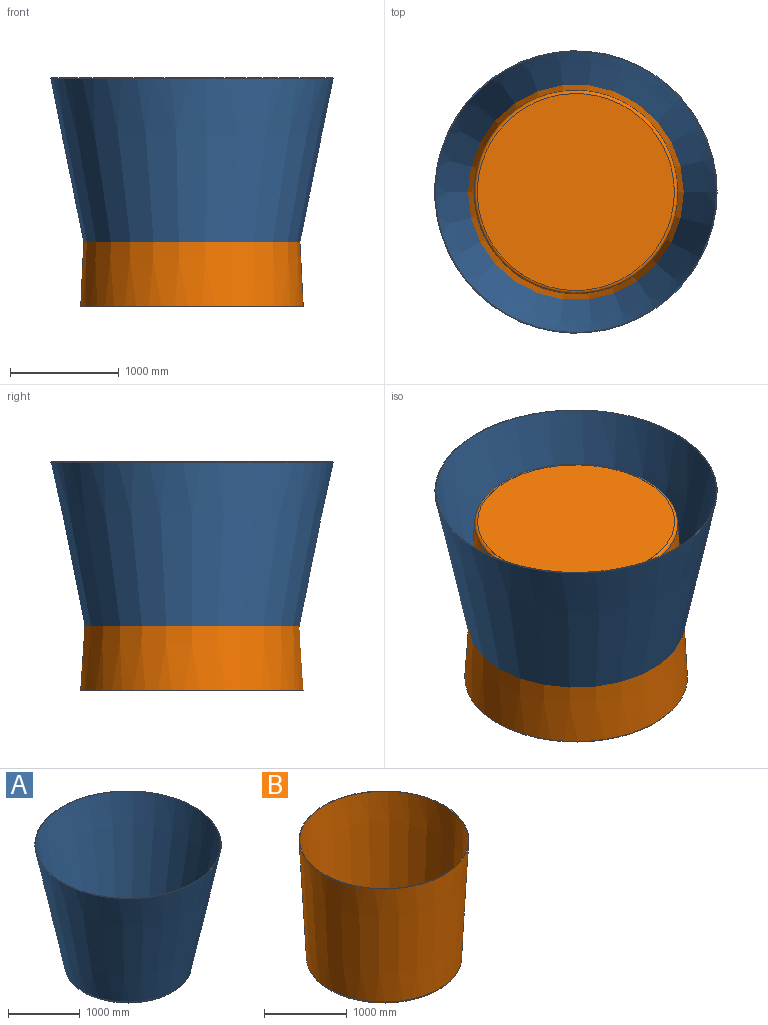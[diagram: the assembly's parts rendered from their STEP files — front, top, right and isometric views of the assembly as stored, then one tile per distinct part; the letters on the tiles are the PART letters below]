
ASSEMBLY  parts=2 mates=1
PART A: 7 faces, bbox 2600x2600x2101.4 mm
  f0: cone r=1300mm half-angle=78.6deg, axis (0,0,-1), area 57026.1mm2, adj f3,f6
  f1: torus R=834.11mm, axis (0,0,1), area 371881.1mm2, adj f2,f3
  f2: plane 1668.21x1668.21mm, normal (0,0,-1), area 2185705.8mm2, adj f1
  f3: cone r=1300mm half-angle=11.4deg, axis (0,0,1), area 14414261.6mm2, adj f0,f1
  f4: torus R=834.11mm, axis (0,0,1), area 318301.6mm2, adj f5,f6
  f5: plane 1668.21x1668.21mm, normal (0,0,1), area 2185705.8mm2, adj f4
  f6: cone r=1293.14mm half-angle=11.4deg, axis (0,0,1), area 14323661.7mm2, adj f0,f4
PART B: 7 faces, bbox 2050x2050x1760 mm
  f0: plane 2050x2050mm, normal (0,0,1), area 44986.4mm2, adj f2,f5
  f1: plane 1812.99x1812.99mm, normal (0,0,-1), area 2581550.3mm2, adj f3
  f2: cone r=1025mm half-angle=2.9deg, axis (0,0,1), area 10683806.5mm2, adj f0,f3
  f3: torus R=906.49mm, axis (0,0,1), area 265038.4mm2, adj f1,f2
  f4: plane 1812.99x1812.99mm, normal (0,0,1), area 2581550.3mm2, adj f6
  f5: cone r=1018.01mm half-angle=2.9deg, axis (0,0,1), area 10605360.2mm2, adj f0,f6
  f6: torus R=906.49mm, axis (0,0,1), area 202236.2mm2, adj f4,f5
PLACE A at identity fixed
PLACE B rot(axis=(1,0,0),180deg) t=(0,0,1760)mm
MATE parallel B.f2 <-> A.f0  axis (0,0,-1) through (0,0,0)mm
